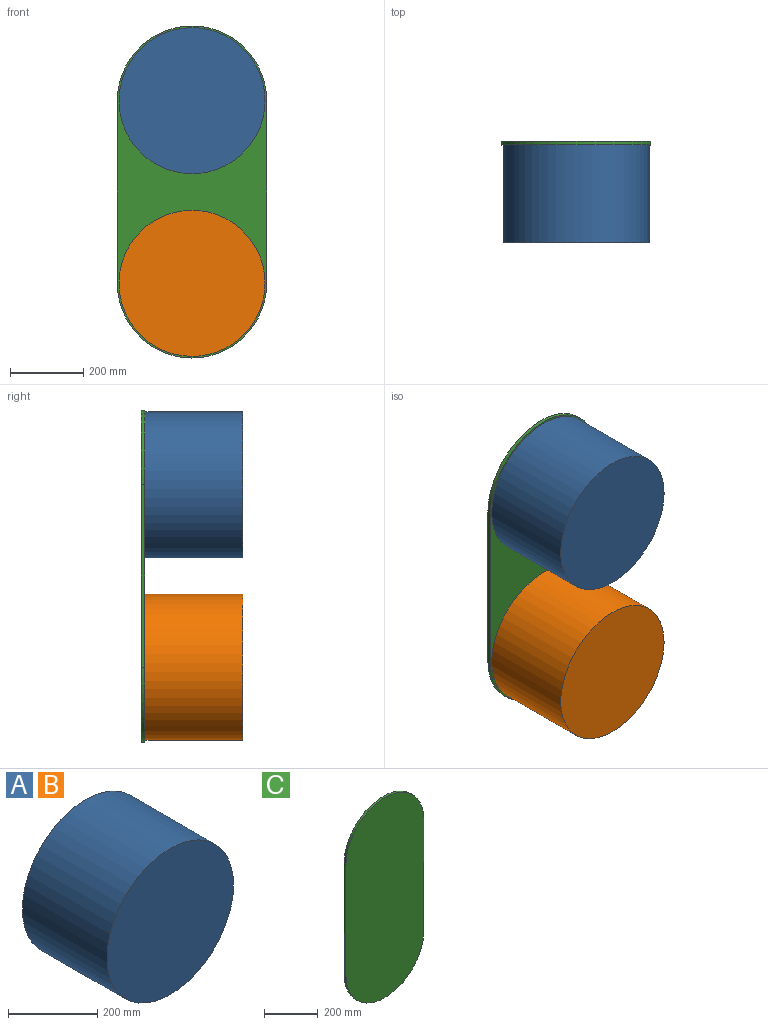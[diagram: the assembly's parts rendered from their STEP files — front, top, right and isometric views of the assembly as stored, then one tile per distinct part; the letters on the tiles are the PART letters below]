
ASSEMBLY  parts=3 mates=2
PART A: 3 faces, bbox 400x267.5x400 mm
  f0: cylinder r=200mm len=400mm, axis (0,1,0), area 336150.4mm2, adj f1,f2
  f1: plane 400x400mm, normal (0,-1,0), area 125663.7mm2, adj f0
  f2: plane 400x400mm, normal (0,1,0), area 125663.7mm2, adj f0
PART B: same geometry as A
PART C: 6 faces, bbox 409.1x10x909.1 mm
  f0: cylinder r=204.55mm len=409.09mm, axis (0,1,0), area 6426mm2, adj f1,f3,f4,f5
  f1: plane 500x10mm, normal (1,0,0), area 5000mm2, adj f0,f2,f4,f5
  f2: cylinder r=204.55mm len=409.09mm, axis (0,1,0), area 6426mm2, adj f1,f3,f4,f5
  f3: plane 500x10mm, normal (-1,0,0), area 5000mm2, adj f0,f2,f4,f5
  f4: plane 909.09x409.09mm, normal (0,-1,0), area 335986mm2, adj f0,f1,f2,f3
  f5: plane 909.09x409.09mm, normal (0,1,0), area 335986mm2, adj f0,f1,f2,f3
PLACE A t=(1272.94,746.98,1071.26)mm
PLACE B t=(1272.94,746.98,571.26)mm
PLACE C t=(1068.39,756.98,920.83)mm
MATE fastened A.f0 <-> C.f2  axis (0,1,0) through (1272.94,746.98,1071.26)mm
MATE fastened B.f0 <-> C.f0  axis (0,1,0) through (1272.94,746.98,571.26)mm
